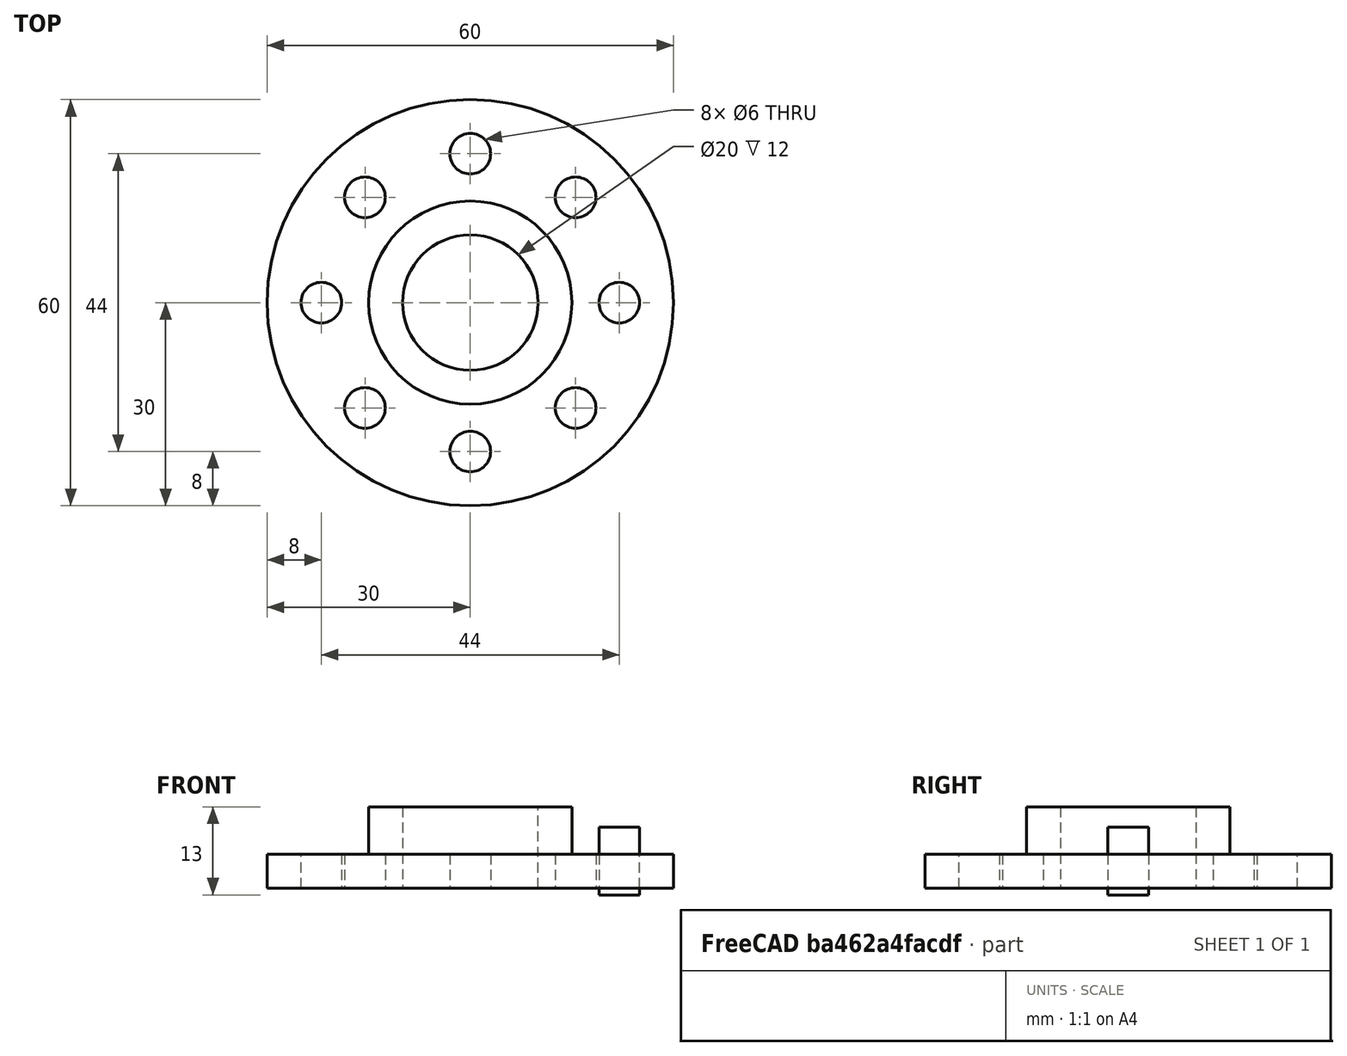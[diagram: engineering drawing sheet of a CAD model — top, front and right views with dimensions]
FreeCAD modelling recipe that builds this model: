
FCSTD DOCUMENT  (FreeCAD 0.20R29603 (Git))
Label: OJT1_T04P05_brida
License: All rights reserved
LicenseURL: http://en.wikipedia.org/wiki/All_rights_reserved
objects: Part::Cylinder×4, Part::Cut×2, Part::MultiFuse×1, Part::FeaturePython×1
note: 7 computed .brp shape members not serialized (recipe doc carries the construction recipe); baked Part::Feature solids carry a one-line shape summary decoded from their .brp

FEATURE [Part::Cylinder] Cylinder  label="Base"
  Angle = 360
  AttacherType = Attacher::AttachEngine3D
  FirstAngle = 0
  Height = 5
  Radius = 30
  SecondAngle = 0
FEATURE [Part::Cylinder] Cylinder001  label="Tub_exterior"
  Angle = 360
  AttacherType = Attacher::AttachEngine3D
  FirstAngle = 0
  Height = 12
  Radius = 15
  SecondAngle = 0
FEATURE [Part::MultiFuse] Fusion
  Shapes = -> [Cylinder001,Cylinder]
FEATURE [Part::Cylinder] Cylinder002  label="Tub_interior"
  Angle = 360
  AttacherType = Attacher::AttachEngine3D
  FirstAngle = 0
  Height = 30
  Placement = pos=(0,0,-2) rot=(0,0,1;0rad)
  Radius = 10
  SecondAngle = 0
FEATURE [Part::Cut] Cut  label="Brida sin taladros"
  Base = -> Fusion
  Tool = -> Cylinder002
FEATURE [Part::Cylinder] Cylinder003  label="Taladro"
  Angle = 360
  AttacherType = Attacher::AttachEngine3D
  FirstAngle = 0
  Height = 10
  Placement = pos=(22,0,-1) rot=(0,0,1;0rad)
  Radius = 3
  SecondAngle = 0
FEATURE [Part::FeaturePython] Array  # Draft array (typed FeaturePython)
  AlwaysSyncPlacement = false
  Angle = 360
  ArrayType = 1
  Axis = (0,0,1)
  Base = -> Cylinder003
  Center = (0,0,0)
  Count = 8
  ExpandArray = false
  Fuse = false
  IntervalAxis = (0,0,0)
  IntervalX = (50,0,0)
  IntervalY = (0,50,0)
  IntervalZ = (0,0,50)
  NumberCircles = 3
  NumberPolar = 8
  NumberX = 2
  NumberY = 2
  NumberZ = 1
  PlacementList = 8 placements: [(22,0,-1),(15.5563,15.5563,-1),(0,22,-1),(-15.5563,15.5563,-1),(-22,2.69422e-15,-1),(-15.5563,-15.5563,-1),(-3.55271e-15,-22,-1),(15.5563,-15.5563,-1)]
  RadialDistance = 50
  ScaleList = (8) [(1,1,1),(1,1,1),(1,1,1),(1,1,1),(1,1,1),(1,1,1),(1,1,1),(1,1,1)]
  Symmetry = 1
  TangentialDistance = 25
FEATURE [Part::Cut] Cut001
  Base = -> Cut
  Tool = -> Array
